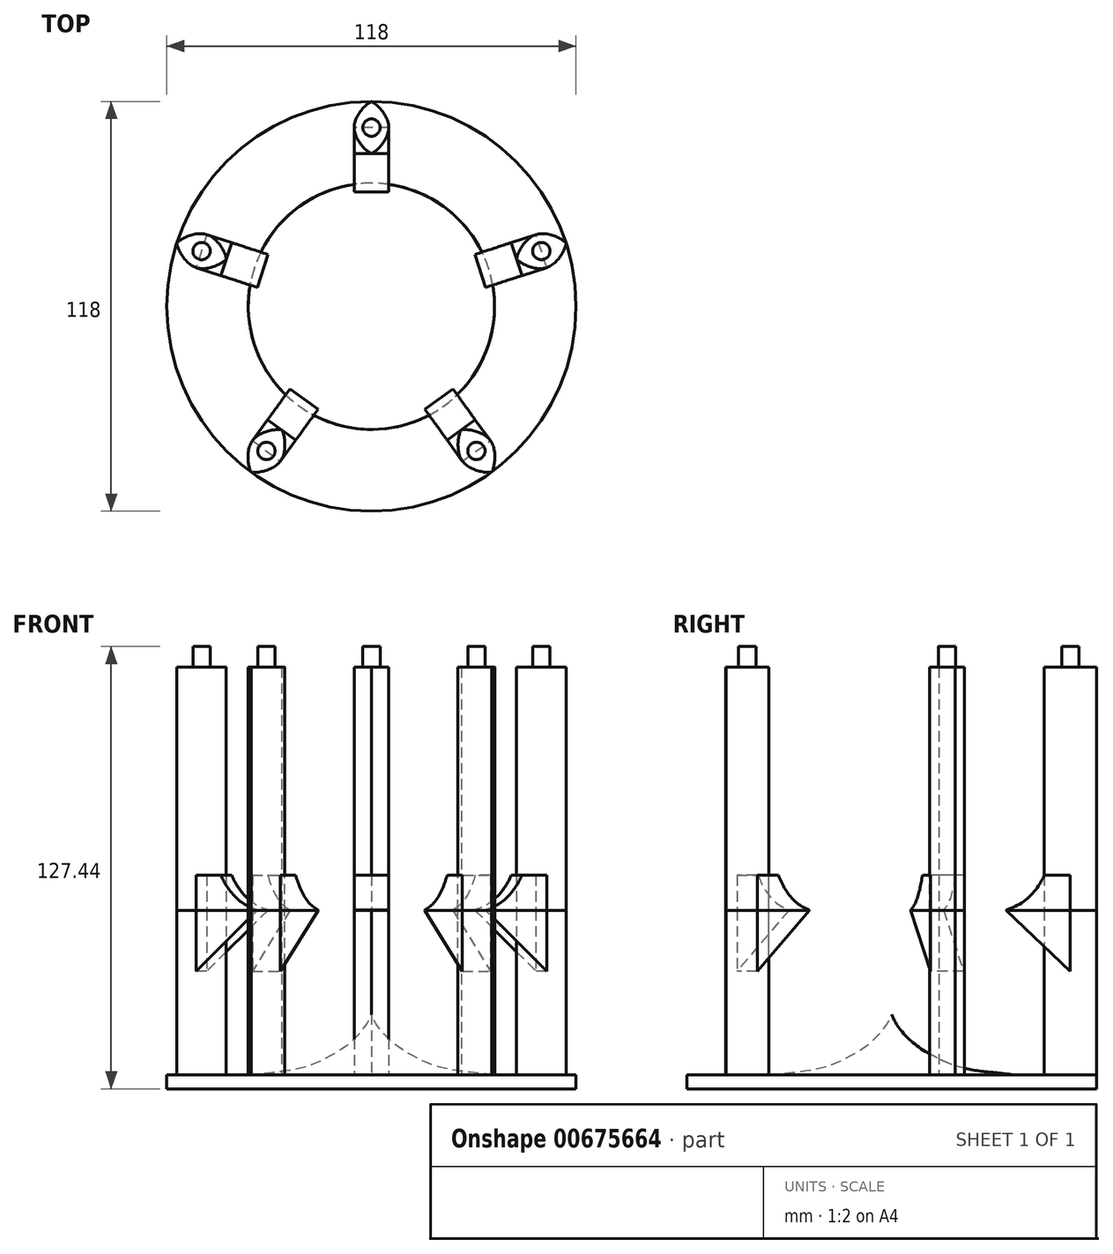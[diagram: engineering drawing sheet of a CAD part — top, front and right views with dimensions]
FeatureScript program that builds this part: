
annotation { "Feature Type Name" : "Feature", "Feature Type Description" : "" }
export const myFeature = defineFeature(function(context is Context, id is Id, definition is map)
    precondition{}
    {
        {
            var Q0;
            Q0=qCreatedBy(makeId("Top.planeOp"),FACE);
            var sketch = newSketch(context, id + "F0", { "sketchPlane" : qUnion([Q0])});
            skCircle(sketch, "E0", {"center": v(0, 0) * mm, "radius": 59 * mm});
            skCircle(sketch, "E1", {"center": v(0, 0) * mm, "radius": 44 * mm});
            skSolve(sketch);
        }
        {
            var Q0;
            Q0=makeQuery(id+"F0.imprint","IMPRINT",FACE,{"disambiguationData":[TD([[makeQuery(id+"F0.imprint","IMPRINT",EDGE,{"derivedFrom":sQuery(id+"F0.wireOp",EDGE,"E0")}),1.0]])]});
            var Q1;
            Q1=makeQuery(id+"F0.imprint","IMPRINT",FACE,{"disambiguationData":[TD([[makeQuery(id+"F0.imprint","IMPRINT",EDGE,{"derivedFrom":sQuery(id+"F0.wireOp",EDGE,"E1")}),1.0]])]});
            extrude(context, id + "F1", {"entities" : qUnion([Q0, Q1]), "depth" : 4.03 * mm, "offsetDistance" : 25 * mm});
        }
        {
            var Q0;
            Q0=makeQuery(id+"F1.opExtrude","CAP_FACE",FACE,{"disambiguationData":[OSD([sQuery(id+"F0.wireOp",EDGE,"E0"),sQuery(id+"F0.wireOp",EDGE,"E1")])],"isStart":false});
            var sketch = newSketch(context, id + "F2", { "sketchPlane" : qUnion([Q0])});
            skFitSpline(sketch, "E2", {"points": [v(0, 59) * mm, v(5, 51.5) * mm, v(0, 44) * mm], "startDerivative": vector(9, -3.6) * mm, "endDerivative": vector(-9, -3.6) * mm});
            skFitSpline(sketch, "E3", {"points": [v(0, 44) * mm, v(-5, 51.5) * mm, v(0, 59) * mm], "startDerivative": vector(-9, 3.6) * mm, "endDerivative": vector(9, 3.6) * mm});
            skLineSegment(sketch, "E4", {"start": v(-5, 51.5) * mm, "end": v(5, 51.5) * mm});
            skLineSegment(sketch, "E5", {"start": v(5, 51.5) * mm, "end": v(5, 33) * mm});
            skLineSegment(sketch, "E6", {"start": v(5, 33) * mm, "end": v(-5, 33) * mm});
            skLineSegment(sketch, "E7", {"start": v(-5, 51.5) * mm, "end": v(-5, 33) * mm});
            skCircle(sketch, "E8", {"center": v(0, 0) * mm, "radius": 44 * mm});
            skSolve(sketch);
        }
        {
            var Q0;
            {var subQ3=sQuery(id+"F2.wireOp",EDGE,"E4");Q0=makeQuery(id+"F2.imprint","IMPRINT",FACE,{"disambiguationData":[TD([[makeQuery(id+"F2.imprint","IMPRINT",EDGE,{"derivedFrom":subQ3}),-1.0]])]});}
            var Q1;
            {var subQ3=sQuery(id+"F2.wireOp",EDGE,"E4");Q1=makeQuery(id+"F2.imprint","IMPRINT",FACE,{"disambiguationData":[TD([[makeQuery(id+"F2.imprint","IMPRINT",EDGE,{"derivedFrom":subQ3}),1.0]])]});}
            extrude(context, id + "F3", {"entities" : qUnion([Q0, Q1]), "operationType" : NewBodyOperationType.ADD, "depth" : 47.4 * mm, "offsetDistance" : 25 * mm});
        }
        {
            var Q0;
            Q0=makeQuery(id+"F3.opExtrude","CAP_FACE",FACE,{"disambiguationData":[OSD([sQuery(id+"F2.wireOp",EDGE,"E2"),sQuery(id+"F2.wireOp",EDGE,"E3")])],"isStart":false});
            var sketch = newSketch(context, id + "F4", { "sketchPlane" : qUnion([Q0])});
            skFitSpline(sketch, "E9", {"points": [v(0, 59) * mm, v(5, 51.5) * mm, v(0, 44) * mm], "startDerivative": vector(9, -3.6) * mm, "endDerivative": vector(-9, -3.6) * mm});
            skFitSpline(sketch, "E10", {"points": [v(0, 44) * mm, v(-5, 51.5) * mm, v(0, 59) * mm], "startDerivative": vector(-9, 3.6) * mm, "endDerivative": vector(9, 3.6) * mm});
            skLineSegment(sketch, "E11", {"start": v(-5, 51.5) * mm, "end": v(5, 51.5) * mm});
            skLineSegment(sketch, "E12", {"start": v(5, 51.5) * mm, "end": v(5, 33) * mm});
            skLineSegment(sketch, "E13", {"start": v(5, 33) * mm, "end": v(-5, 33) * mm});
            skLineSegment(sketch, "E14", {"start": v(-5, 51.5) * mm, "end": v(-5, 33) * mm});
            skCircle(sketch, "E15", {"center": v(0, 0) * mm, "radius": 44 * mm});
            skSolve(sketch);
        }
        {
            var Q0;
            {var subQ5=sQuery(id+"F4.wireOp",EDGE,"E13");Q0=makeQuery(id+"F4.imprint","IMPRINT",FACE,{"disambiguationData":[TD([[makeQuery(id+"F4.imprint","IMPRINT",EDGE,{"derivedFrom":subQ5}),-1.0]])]});}
            var Q1;
            {var subQ0=sQuery(id+"F4.wireOp",EDGE,"E15");var subQ3=sQuery(id+"F4.wireOp",EDGE,"E12");var subQ5=makeQuery(id+"F4.imprint","INTERSECT",VERTEX,{"derivedFrom":[subQ3,subQ0]});Q1=makeQuery(id+"F4.imprint","IMPRINT",FACE,{"disambiguationData":[TD([[makeQuery(id+"F4.imprint","IMPRINT",EDGE,{"disambiguationData":[TD([[subQ5,1.0]])],"derivedFrom":subQ3}),-1.0]])]});}
            var Q2;
            {var subQ0=sQuery(id+"F4.wireOp",EDGE,"E15");var subQ3=sQuery(id+"F4.wireOp",EDGE,"E14");var subQ5=makeQuery(id+"F4.imprint","INTERSECT",VERTEX,{"derivedFrom":[subQ3,subQ0]});Q2=makeQuery(id+"F4.imprint","IMPRINT",FACE,{"disambiguationData":[TD([[makeQuery(id+"F4.imprint","IMPRINT",EDGE,{"disambiguationData":[TD([[subQ5,1.0]])],"derivedFrom":subQ3}),1.0]])]});}
            extrude(context, id + "F5", {"entities" : qUnion([Q0, Q1, Q2]), "operationType" : NewBodyOperationType.ADD, "depth" : 0.1 * mm, "offsetDistance" : 25 * mm});
        }
        {
            var Q0;
            Q0=makeQuery(id+"F5.opExtrude","SWEPT_FACE",FACE,{"disambiguationData":[OSD([sQuery(id+"F4.wireOp",EDGE,"E14")])]});
            var sketch = newSketch(context, id + "F6", { "sketchPlane" : qUnion([Q0])});
            skLineSegment(sketch, "E16", {"start": v(-51.5, 51.54) * mm, "end": v(-51.5, 0) * mm});
            skLineSegment(sketch, "E17", {"start": v(-33, 51.44) * mm, "end": v(-51.5, 33.92) * mm});
            skSolve(sketch);
        }
        {
            var Q0;
            {var subQ2=sQuery(id+"F6.wireOp",EDGE,"E17");Q0=makeQuery(id+"F6.imprint","IMPRINT",FACE,{"disambiguationData":[TD([[makeQuery(id+"F6.imprint","IMPRINT",EDGE,{"derivedFrom":subQ2}),-1.0]])]});}
            extrude(context, id + "F7", {"entities" : qUnion([Q0]), "depth" : -10 * mm, "offsetDistance" : 25 * mm});
        }
        {
            var Q0;
            Q0=makeQuery(id+"F5.opExtrude","SWEPT_FACE",FACE,{"disambiguationData":[OSD([sQuery(id+"F4.wireOp",EDGE,"E14")])]});
            var sketch = newSketch(context, id + "F8", { "sketchPlane" : qUnion([Q0])});
            skLineSegment(sketch, "E18", {"start": v(-51.5, 61.54) * mm, "end": v(-51.5, 51.54) * mm});
            skLineSegment(sketch, "E19", {"start": v(-51.5, 61.54) * mm, "end": v(-44, 61.54) * mm});
            skFitSpline(sketch, "E20", {"points": [v(-44, 61.54) * mm, v(-42.6, 58.94) * mm, v(-40.2, 55.84) * mm, v(-36.9, 53.24) * mm, v(-33, 51.54) * mm], "startDerivative": vector(5.6, -12.97) * mm, "endDerivative": vector(15.44, -5.36) * mm});
            skSolve(sketch);
        }
        {
            var Q0;
            Q0=makeQuery(id+"F8.imprint","IMPRINT",FACE,{"disambiguationData":[TD([[makeQuery(id+"F8.imprint","IMPRINT",EDGE,{"derivedFrom":sQuery(id+"F8.wireOp",EDGE,"E18")}),1.0]])]});
            extrude(context, id + "F9", {"entities" : qUnion([Q0]), "operationType" : NewBodyOperationType.ADD, "depth" : -10 * mm, "offsetDistance" : 25 * mm});
        }
        {
            var Q0;
            Q0=makeQuery(id+"F3.opExtrude","CAP_FACE",FACE,{"disambiguationData":[OSD([sQuery(id+"F2.wireOp",EDGE,"E2"),sQuery(id+"F2.wireOp",EDGE,"E3")])],"isStart":false});
            var sketch = newSketch(context, id + "F10", { "sketchPlane" : qUnion([Q0])});
            skFitSpline(sketch, "E21", {"points": [v(0, 64) * mm, v(7.5, 54) * mm, v(0, 44) * mm], "startDerivative": vector(9, -3.6) * mm, "endDerivative": vector(-9, -3.6) * mm});
            skFitSpline(sketch, "E22", {"points": [v(0, 44) * mm, v(-7.5, 54) * mm, v(0, 64) * mm], "startDerivative": vector(-9, 3.6) * mm, "endDerivative": vector(9, 3.6) * mm});
            skCircle(sketch, "E23", {"center": v(0, 0) * mm, "radius": 44 * mm});
            skSolve(sketch);
        }
        {
            var Q0;
            Q0=makeQuery(id+"F10.imprint","IMPRINT",FACE,{"disambiguationData":[TD([[makeQuery(id+"F10.imprint","IMPRINT",EDGE,{"derivedFrom":sQuery(id+"F10.wireOp",EDGE,"E21")}),-1.0]])]});
            extrude(context, id + "F11", {"entities" : qUnion([Q0]), "depth" : 70 * mm, "offsetDistance" : 25 * mm});
        }
        {
            var Q0;
            Q0=makeQuery(id+"F11.opExtrude","CAP_FACE",FACE,{"disambiguationData":[OSD([sQuery(id+"F10.wireOp",EDGE,"E21"),sQuery(id+"F10.wireOp",EDGE,"E22")])],"isStart":false});
            var sketch = newSketch(context, id + "F12", { "sketchPlane" : qUnion([Q0])});
            skCircle(sketch, "E24", {"center": v(0, 51.5) * mm, "radius": 2.5 * mm});
            skLineSegment(sketch, "E25", {"start": v(0, 0) * mm, "end": v(0, 44) * mm});
            skSolve(sketch);
        }
        {
            var Q0;
            Q0=makeQuery(id+"F12.imprint","IMPRINT",FACE,{"disambiguationData":[TD([[makeQuery(id+"F12.imprint","IMPRINT",EDGE,{"derivedFrom":sQuery(id+"F12.wireOp",EDGE,"E24")}),1.0]])]});
            extrude(context, id + "F13", {"entities" : qUnion([Q0]), "depth" : 6 * mm, "offsetDistance" : 25 * mm});
        }
        {
            var Q0;
            Q0=qCreatedBy(makeId("Right.planeOp"),FACE);
            var sketch = newSketch(context, id + "F14", { "sketchPlane" : qUnion([Q0])});
            skLineSegment(sketch, "E26", {"start": v(0, 0) * mm, "end": v(44, 4.03) * mm});
            skLineSegment(sketch, "E27", {"start": v(0, 0) * mm, "end": v(-44, 4.03) * mm});
            skLineSegment(sketch, "E28", {"start": v(0, 0) * mm, "end": v(0, 21.45) * mm});
            skLineSegment(sketch, "E29", {"start": v(0, 0) * mm, "end": v(35.5, 4.03) * mm});
            skLineSegment(sketch, "E30", {"start": v(35.5, 4.03) * mm, "end": v(0, 4.03) * mm});
            skFitSpline(sketch, "E31", {"points": [v(35.5, 4.03) * mm, v(26.22, 5.03) * mm, v(18.5, 6.58) * mm, v(12.03, 9.43) * mm, v(6.85, 12.73) * mm, v(2.4, 17.13) * mm, v(0, 21.45) * mm], "startDerivative": vector(-68.57, 8.12) * mm, "endDerivative": vector(-13.37, 35.14) * mm});
            skSolve(sketch);
        }
        {
            var Q0;
            {var subQ2=sQuery(id+"F14.wireOp",EDGE,"E30");Q0=makeQuery(id+"F14.imprint","IMPRINT",FACE,{"disambiguationData":[TD([[makeQuery(id+"F14.imprint","IMPRINT",EDGE,{"derivedFrom":subQ2}),-1.0]])]});}
            var Q1;
            Q1=makeQuery(id+"F1.opExtrude","SWEPT_FACE",FACE,{"disambiguationData":[OSD([sQuery(id+"F0.wireOp",EDGE,"E0")])]});
            revolve(context, id + "F15", {"operationType" : NewBodyOperationType.ADD, "entities" : qUnion([Q0]), "axis" : qUnion([Q1]), "revolveType" : RevolveType.FULL});
        }
        {
            var Q0;
            Q0=makeQuery(id+"F1.opExtrude","SWEPT_BODY",BODY,{"disambiguationData":[OSD([sQuery(id+"F0.wireOp",EDGE,"E0")])]});
            var Q1;
            Q1=makeQuery(id+"F7.opExtrude","SWEPT_BODY",BODY,{"disambiguationData":[OSD([sQuery(id+"F4.wireOp",EDGE,"E14"),sQuery(id+"F6.wireOp",EDGE,"E16"),sQuery(id+"F6.wireOp",EDGE,"E17")])]});
            var Q2;
            Q2=makeQuery(id+"F5.opExtrude","SWEPT_BODY",BODY,{"disambiguationData":[OSD([sQuery(id+"F4.wireOp",EDGE,"E9"),sQuery(id+"F4.wireOp",EDGE,"E10"),sQuery(id+"F4.wireOp",EDGE,"E12"),sQuery(id+"F4.wireOp",EDGE,"E13"),sQuery(id+"F4.wireOp",EDGE,"E14")])]});
            var Q3;
            Q3=makeQuery(id+"F11.opExtrude","SWEPT_BODY",BODY,{"disambiguationData":[OSD([sQuery(id+"F10.wireOp",EDGE,"E21"),sQuery(id+"F10.wireOp",EDGE,"E22")])]});
            var Q4;
            Q4=makeQuery(id+"F13.opExtrude","SWEPT_BODY",BODY,{"disambiguationData":[OSD([sQuery(id+"F12.wireOp",EDGE,"E24")])]});
            var Q5;
            Q5=makeQuery(id+"F1.opExtrude","CAP_EDGE",EDGE,{"disambiguationData":[OSD([sQuery(id+"F0.wireOp",EDGE,"E0")])],"isStart":true});
            circularPattern(context, id + "F16", {"entities" : qUnion([Q0, Q1, Q2, Q3, Q4]), "axis" : qUnion([Q5]), "angle" : 360 * degree, "instanceCount" : 5, "equalSpace" : true});
        }
    });
